# Revit family: QF_ELECTROLUXPROFESSIONAL_1LSNSS_TD6-30_G
name_source: partatom
category: Attrezzature speciali
units: mm (PartAtom-declared; Revit-internal decimal feet)

## family parameters
Basato su piano di lavoro = No
Condiviso = No
Punto di calcolo locali = No
Quota connettore circolare = Usa diametro
Sempre verticale = Sì
Taglio con vuoti quando caricato = No
Tipo di parte = Normale

## types (36) — shared parameters
Depth Actual = 1365 mm  [stored 4.47835 ft]
Height Actual = 1855 mm  [stored 6.08596 ft]
Latent Heat Output = 0.0
Length Actual = 960 mm  [stored 3.14961 ft]
Modello = TD6-30
Produttore = Electrolux Professional
Sensible Heat Output = 0.0
URL = www.electroluxprofessional.com
Weight = 280
zero-valued in all types: Prospetto di default, Steam Pounds per Hour

## per-type parameters (varying)
| type | Cycle | Descrizione | Gas KW | Item Number | Phase | Volts | Watts |
| 9872330088 | 60 Hz | TUMBLE DRYER TD6-30 30KG GALVA.DRUM GAS 33KW 480/60/3 COMPASS PRO 6G81 SLVR/SLVR DO.LEFT REV MB DISCON DMPR | 33 | 1L826J | 3 | 480 V | 1500 W |
| 9872330040 | 50 Hz | TUMBLE DRYER TD6-30 30KG SST DRUM GAS 33KW 380-415/50/3N COMPASS PRO 6L80 SLVR/SLVR DO.RIGHT REV DMPR | 33 | 1L0G5P | 3 | 415 V | 1500 W |
| 9872330060 | 50 Hz | TUMBLE DRYER TD6-30 30KG GALVA.DRUM GAS 33KW 220/50/1 COMPASS PRO 6L80 SLVR/SLVR DO.RIGHT REV DISCON DMPR | 33 | 1L0GAW | 1 | 220 V | 1700 W |
| 9872330078 | 50 Hz | TUMBLE DRYER TD6-30 30KG GALVA.DRUM GAS 33KW 240/50/1 COMPASS PRO 6L80 2.I/O SLVR/SLVR DO.RIGHT ELS-NETW. REV DMPR | 33 | 1L0GKD | 1 | 240 V | 1700 W |
| 9872330015 | 60 Hz | TUMBLE DRYER TD6-30 30KG GALVA.DRUM GAS 33KW 230/60/3 COMPASS PRO 6G82 SLVR/SLVR DO.RIGHT REV DISCON DMPR | 33 | 1L0G53 | 3 | 230 V | 1500 W |
| 9872330109 | 60 Hz | TUMBLE DRYER TD6-30 30KG SST DRUM GAS 33KW 220/60/3 COMPASS PRO 6G81 SLVR/SLVR DO.RIGHT REV MB DISCON DMPR | 33 | 1LSPLN | 3 | 220 V | 1500 W |
| 9872330129 | 60 Hz | TUMBLE DRYER TD6-30 30KG SST DRUM GPL 33KW 200/60/3 COMPASS PRO 6G86 SLVR/SLVR DO.RIGHT REV DISCON DMPR | 0 | 1LT5Z7 | 3 | 200 V | 1500 W |
| 9872330149 | 60 Hz | TUMBLE DRYER TD6-30 30KG SST DRUM GPL 33KW 200/60/3 COMPASS PRO 6L85 SST/SLVR DO.RIGHT REV DISCON DMPR | 0 | 1L0HAA | 3 | 200 V | 1500 W |
| 9872330159 | 50 Hz | TUMBLE DRYER TD6-30 30KG SST DRUM GAS 33KW 380-415/50/3N COMPASS PRO 6G81 SST/SST DO.RIGHT REV MB STOP DISCON DMPR | 0 | 1LT65P | 3 | 415 V | 1500 W |
| 9872330002 | 50 Hz | TUMBLE DRYER TD6-30 30KG GALVA.DRUM GAS 33KW 380-415/50/3N COMPASS PRO 6G81 SLVR/SLVR DO.RIGHT REV MB STOP DISCON DMPR | 33 | 1L0G4Y | 3 | 415 V | 1500 W |
| 9872330062 | 50 Hz | TUMBLE DRYER TD6-30 30KG SST DRUM GAS 33KW 380-415/50/3N COMPASS PRO 6G81 SST/SLVR DO.RIGHT REV MB STOP DISCON DMPR | 33 | 1L0GCJ | 3 | 415 V | 1500 W |
| 9872330087 | 50 Hz | TUMBLE DRYER TD6-30 30KG SST DRUM GAS 33KW 230/50/1 COMPASS PRO 6G82 SLVR/SLVR DO.RIGHT REV STOP DISCON DMPR | 33 | 1L0GTL | 1 | 230 V | 1700 W |
| 9872330133 | 50 Hz | TUMBLE DRYER TD6-30 30KG SST DRUM GPL 33KW 200/50/3 COMPASS PRO 6G86 SLVR/SLVR DO.RIGHT REV DISCON DMPR | 0 | 1LT5Z8 | 3 | 200 V | 1500 W |
| 9872330143 | 50 Hz | TUMBLE DRYER TD6-30 30KG SST DRUM GPL 33KW 200/50/3 COMPASS PRO 6L85 SLVR/SLVR DO.RIGHT REV DISCON DMPR | 0 | 1LT613 | 3 | 200 V | 1500 W |
| 9872330007 | 50 Hz | TUMBLE DRYER TD6-30 30KG GALVA.DRUM GAS 33KW 380-415/50/3N COMPASS PRO 6G82 SLVR/SLVR DO.RIGHT REV DISCON DMPR | 33 | 1L0G3D | 3 | 415 V | 1500 W |
| 9872330017 | 50 Hz | TUMBLE DRYER TD6-30 30KG GALVA.DRUM GAS 33KW 230/50/1 COMPASS PRO 6G81 SLVR/SLVR DO.RIGHT REV MB DISCON DMPR | 33 | 1L0G55 | 1 | 230 V | 1700 W |
| 9872330084 | 60 Hz | TUMBLE DRYER TD6-30 30KG GALVA.DRUM GAS 33KW 230/60/3 COMPASS PRO 6L80 SLVR/SLVR DO.LEFT REV DMPR | 33 | 1L0GRB | 3 | 230 V | 1500 W |
| 9872330146 | 50 Hz | TUMBLE DRYER TD6-30 30KG SST DRUM GPL 33KW 200/50/3 COMPASS PRO 6L85 SST/SLVR DO.RIGHT REV DISCON DMPR | 0 | 1L0H96 | 3 | 200 V | 1500 W |
| 9872330014 | 50 Hz | TUMBLE DRYER TD6-30 30KG SST DRUM GAS 33KW 380-415/50/3N COMPASS PRO 6G81 SLVR/SLVR DO.RIGHT REV MB STOP DISCON DMPR | 33 | 1L0G3K | 3 | 415 V | 1500 W |
| 9872330054 | 50 Hz | TUMBLE DRYER TD6-30 30KG GALVA.DRUM GAS 33KW 380-415/50/3N COMPASS PRO 6L80 2.I/O SLVR/SLVR DO.RIGHT EXT.PM. REV DMPR | 33 | 1LSP6R | 3 | 415 V | 1500 W |
| 9872330074 | 60 Hz | TUMBLE DRYER TD6-30 30KG GALVA.DRUM GAS 33KW 208-240/60/3 COMPASS PRO 6G81 SLVR/SLVR DO.LEFT REV MB STOP DISCON DMPR | 33 | 1L0GEF | 3 | 240 V | 25500 W |
| 9872330001 | 50 Hz | TUMBLE DRYER TD6-30 30KG GALVA.DRUM GAS 33KW 380-415/50/3N COMPASS PRO 6G82 SLVR/SLVR DO.RIGHT REV DMPR | 33 | 1L0G4X | 3 | 415 V | 1500 W |
| 9872330011 | 50 Hz | TUMBLE DRYER TD6-30 30KG GALVA.DRUM GAS 33KW 380-415/50/3N COMPASS PRO 6G81 SLVR/SLVR DO.RIGHT REV MB STOP DISCON DMPR | 33 | 1L0G3H | 3 | 415 V | 1500 W |
| 9872330031 | 50 Hz | TUMBLE DRYER TD6-30 30KG SST DRUM GAS 33KW 220/50/1 COMPASS PRO 6L85 SLVR/SLVR DO.RIGHT REV DMPR | 33 | 1L0G5K | 1 | 220 V | 1700 W |
| 9872330135 | 60 Hz | TUMBLE DRYER TD6-30 30KG SST DRUM GPL 33KW 200/60/3 COMPASS PRO 6L85 SLVR/SLVR DO.RIGHT REV DISCON DMPR | 0 | 1LT5ZA | 3 | 200 V | 1500 W |
| 9872330061 | 50 Hz | TUMBLE DRYER TD6-30 30KG GALVA.DRUM GAS 33KW 380-415/50/3N COMPASS PRO 6L80 SLVR/SLVR DO.RIGHT REV DISCON DMPR | 33 | 1L0GAX | 3 | 415 V | 1500 W |
| 9872330029 | 50 Hz | TUMBLE DRYER TD6-30 30KG SST DRUM GAS 33KW 380-415/50/3N COMPASS PRO 6G82 SLVR/SLVR DO.RIGHT REV STOP DISCON DMPR | 33 | 1L0G5H | 3 | 415 V | 1500 W |
| 9872330096 | 60 Hz | TUMBLE DRYER TD6-30 30KG SST DRUM GAS 33KW 380-415/60/3 COMPASS PRO 6G82 SST/SST DO.RIGHT REV STOP DISCON DMPR | 33 | 1LSPFZ | 3 | 415 V | 1500 W |
| 9872330148 | 60 Hz | TUMBLE DRYER TD6-30 30KG GALVA.DRUM GAS 33KW 220/60/3 COMPASS PRO 6G82 SLVR/SLVR DO.RIGHT REV STOP DISCON DMPR | 0 | 1L0H9M | 3 | 220 V | 1500 W |
| 9872330056 | 50 Hz | TUMBLE DRYER TD6-30 30KG GALVA.DRUM GAS 33KW 230/50/1 COMPASS PRO 6G82 SLVR/SLVR DO.RIGHT ELS-NETW. REV DISCON DMPR | 33 | 1L0G9A | 1 | 230 V | 1700 W |
| 9872330076 | 60 Hz | TUMBLE DRYER TD6-30 30KG GALVA.DRUM GAS 33KW 220/60/1 COMPASS PRO 6G82 SLVR/SLVR DO.RIGHT REV DISCON DMPR | 33 | 1L0GFX | 1 | 220 V | 1700 W |
| 9872330158 | 60 Hz | TUMBLE DRYER TD6-30 30KG GALVA.DRUM GAS 33KW 220/60/3 COMPASS PRO 6G82 SLVR/SLVR DO.LEFT REV DISCON DMPR | 0 | 1LT65N | 3 | 220 V | 1500 W |
| 9872330003 | 50 Hz | TUMBLE DRYER TD6-30 30KG GALVA.DRUM GAS 33KW 240/50/1 COMPASS PRO 6G81 SLVR/SLVR DO.RIGHT REV MB STOP DISCON DMPR | 33 | 1L0G3C | 1 | 240 V | 1700 W |
| 9872330013 | 50 Hz | TUMBLE DRYER TD6-30 30KG GALVA.DRUM GAS 33KW 380-415/50/3N COMPASS PRO 6G82 SLVR/SLVR DO.RIGHT REV STOP DISCON DMPR | 33 | 1L0G52 | 3 | 415 V | 1500 W |
| 9872330147 | 60 Hz | TUMBLE DRYER TD6-30 30KG GALVA.DRUM GAS 33KW 220/60/3 COMPASS PRO 6G81 SLVR/SLVR DO.RIGHT REV MB STOP DISCON DMPR | 0 | 1L0H9L | 3 | 220 V | 1500 W |
| 9872330152 | 50 Hz | TUMBLE DRYER TD6-30 30KG SST DRUM GAS 33KW 380-415/50/3N COMPASS PRO 6G82 SST/SST DO.RIGHT REV STOP DISCON DMPR | 0 | 1LT64H | 3 | 415 V | 1500 W |

note: [stored X ft] marks values corroborated as IEEE doubles in the binary element streams (Revit-internal decimal feet)

## geometry (parser evidence)
native form markers: Blend x8
no freeform markers — native parametric forms only
